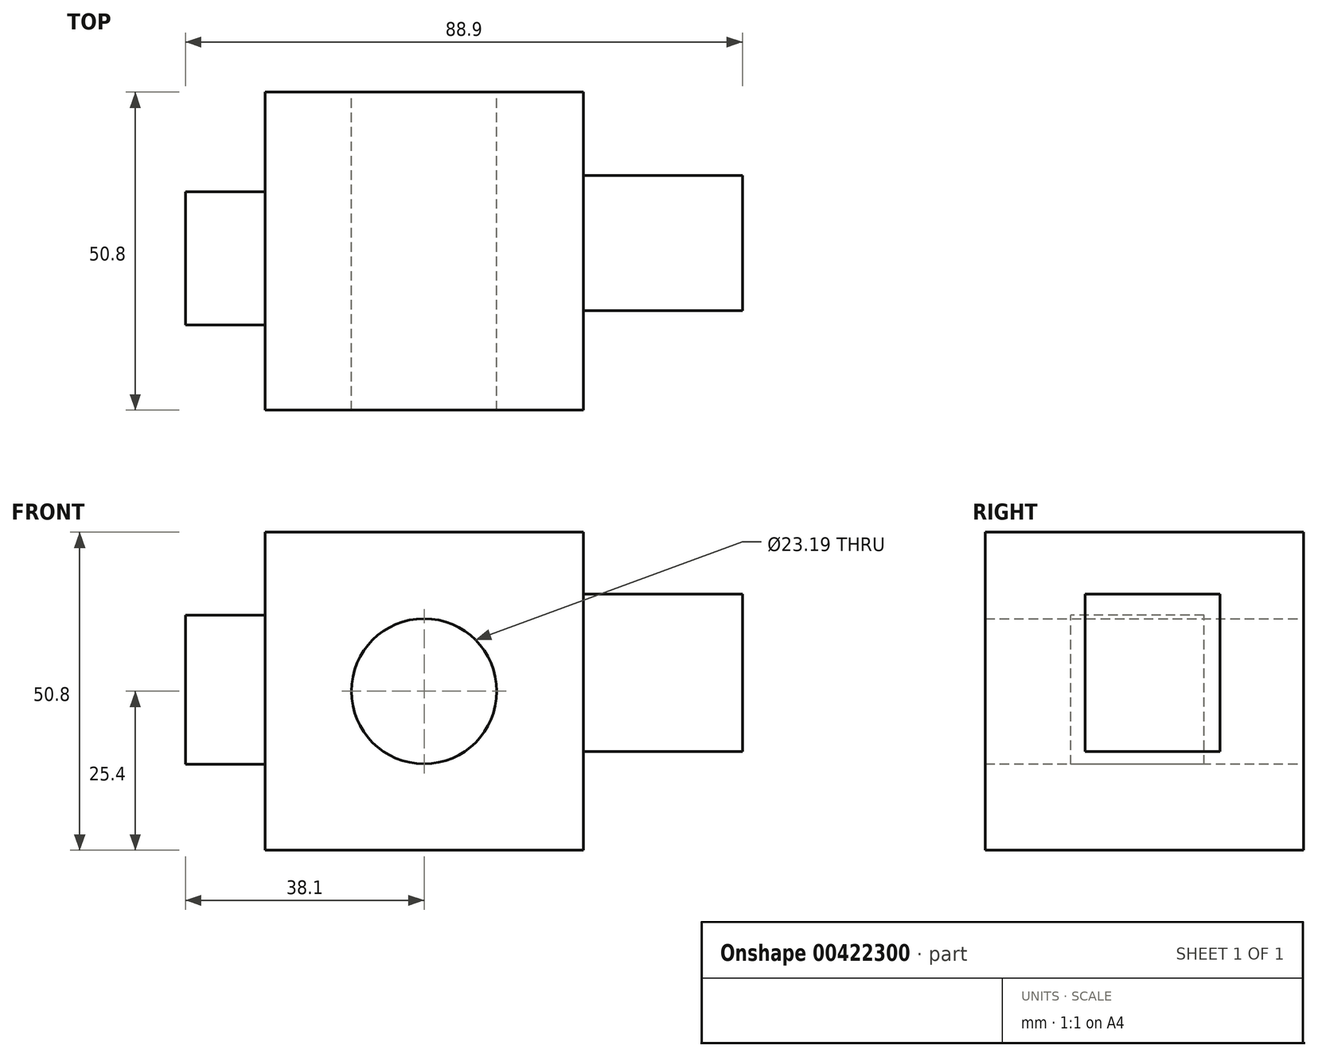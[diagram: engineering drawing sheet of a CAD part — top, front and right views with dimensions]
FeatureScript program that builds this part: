
annotation { "Feature Type Name" : "Feature", "Feature Type Description" : "" }
export const myFeature = defineFeature(function(context is Context, id is Id, definition is map)
    precondition{}
    {
        {
            var Q0;
            Q0=qCreatedBy(makeId("Front.planeOp"),FACE);
            var sketch = newSketch(context, id + "F0", { "sketchPlane" : qUnion([Q0])});
            skLineSegment(sketch, "E0.bottom", {"start": v(0, 0) * mm, "end": v(-50.8, 0) * mm});
            skLineSegment(sketch, "E0.top", {"start": v(0, 50.8) * mm, "end": v(-50.8, 50.8) * mm});
            skLineSegment(sketch, "E0.left", {"start": v(0, 0) * mm, "end": v(0, 50.8) * mm});
            skLineSegment(sketch, "E0.right", {"start": v(-50.8, 0) * mm, "end": v(-50.8, 50.8) * mm});
            skCircle(sketch, "E1", {"center": v(-25.4, 25.4) * mm, "radius": 11.6 * mm});
            skSolve(sketch);
        }
        {
            var Q0;
            Q0 = qSketchRegion(id + "F0", true);
            extrude(context, id + "F1", {"entities" : qUnion([Q0]), "depth" : 50.8 * mm});
        }
        {
            var Q0;
            Q0=makeQuery(id+"F1.opExtrude","SWEPT_FACE",FACE,{"disambiguationData":[OSD([sQuery(id+"F0.wireOp",EDGE,"E0.left")])]});
            var sketch = newSketch(context, id + "F2", { "sketchPlane" : qUnion([Q0])});
            skLineSegment(sketch, "E2.bottom", {"start": v(-34.88, 15.77) * mm, "end": v(-13.33, 15.77) * mm});
            skLineSegment(sketch, "E2.top", {"start": v(-34.88, 40.9) * mm, "end": v(-13.33, 40.9) * mm});
            skLineSegment(sketch, "E2.left", {"start": v(-34.88, 15.77) * mm, "end": v(-34.88, 40.9) * mm});
            skLineSegment(sketch, "E2.right", {"start": v(-13.33, 15.77) * mm, "end": v(-13.33, 40.9) * mm});
            skSolve(sketch);
        }
        {
            var Q0;
            Q0 = qSketchRegion(id + "F2", true);
            extrude(context, id + "F3", {"entities" : qUnion([Q0]), "operationType" : NewBodyOperationType.ADD, "depth" : 25.4 * mm});
        }
        {
            var Q0;
            Q0=makeQuery(id+"F1.opExtrude","SWEPT_FACE",FACE,{"disambiguationData":[OSD([sQuery(id+"F0.wireOp",EDGE,"E0.right")])]});
            var sketch = newSketch(context, id + "F4", { "sketchPlane" : qUnion([Q0])});
            skLineSegment(sketch, "E3.bottom", {"start": v(15.9, 13.72) * mm, "end": v(37.18, 13.72) * mm});
            skLineSegment(sketch, "E3.top", {"start": v(15.9, 37.57) * mm, "end": v(37.18, 37.57) * mm});
            skLineSegment(sketch, "E3.left", {"start": v(15.9, 13.72) * mm, "end": v(15.9, 37.57) * mm});
            skLineSegment(sketch, "E3.right", {"start": v(37.18, 13.72) * mm, "end": v(37.18, 37.57) * mm});
            skSolve(sketch);
        }
        {
            var Q0;
            Q0 = qSketchRegion(id + "F4", true);
            extrude(context, id + "F5", {"entities" : qUnion([Q0]), "operationType" : NewBodyOperationType.ADD, "depth" : 12.7 * mm});
        }
    });
